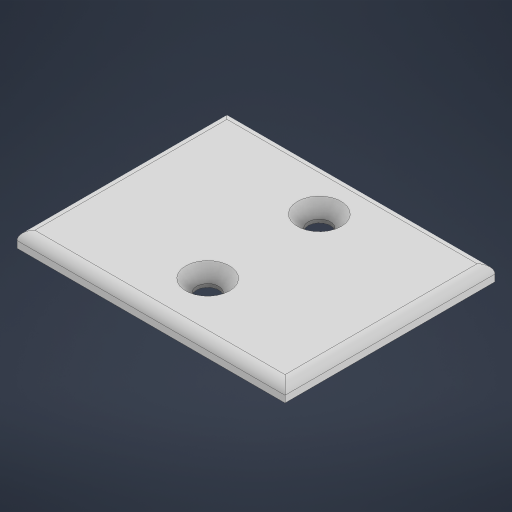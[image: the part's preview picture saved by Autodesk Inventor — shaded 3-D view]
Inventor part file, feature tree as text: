
AUTODESK INVENTOR PART (.ipt)
format: ipt  version: 2024 (Build 280153000, 153)  size: 189,440 bytes
history: native  units: in
note: dims shown in document units (in); Inventor stores cm internally (conversion verified against a paired STEP export)
features: sketch x2, extrude x1, hole x1, fillet x1
ambient origin geometry x8: Origin, YZ Plane, XZ Plane, XY Plane, X Axis, Y Axis, Z Axis, Center Point
bodies: Solid1 (feature_tree)
feature tree (5):
  extrude  "Extrusion1"  Depth=1.8504in
  hole  "Hole1"  [1 undecoded]
  fillet  "Fillet2"  Radius=0.4724in
  sketch  "Sketch1"  dims[d0=2.3622in d1=1.8504in]
  sketch  "Sketch2"  dims[d7=0.1378in d8=0.0in d10=0.9843in d11=0.4724in d12=0.3937in d13=0.196in d14=0.2362in d15=0.385in d16=0.0787in d17=0.5635in d18=0.315in d19=0.8108in d20=0.0787in]
note: 1 required parameter value undecoded (feature->parameter linkage not recoverable at this tier; creation-order binding heuristic only, values carry confidence <= 0.55)
